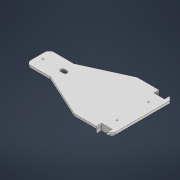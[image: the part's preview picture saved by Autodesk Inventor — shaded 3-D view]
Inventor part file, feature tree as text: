
AUTODESK INVENTOR PART (.ipt)
format: ipt  version: 2022 (Build 260153000, 153)  size: 181,760 bytes
history: native  units: in
note: dims shown in document units (in); Inventor stores cm internally (conversion verified against a paired STEP export)
features: sketch x9, extrude x6, fillet x2, chamfer x2, hole x1
ambient origin geometry x8: Origin, YZ Plane, XZ Plane, XY Plane, X Axis, Y Axis, Z Axis, Center Point
bodies: Solid1 (feature_tree)
feature tree (20):
  extrude  "Extrusion1"  Depth=0.7874in
  fillet  "Fillet1"  Radius=3.937in
  fillet  "Fillet2"  Radius=0.7874in
  chamfer  "Chamfer1"  Distance=1.5748in Angle=45.0deg
  chamfer  "Chamfer2"  Distance=1.5748in Angle=45.0deg
  sketch  "Sketch3"  dims[d19=1.9685in]
  sketch  "Sketch4"  dims[d20=1.9685in d21=1.5748in d22=0.0787in d23=45.0deg d24=1.5748in d25=0.0787in d26=45.0deg]
  extrude  "Extrusion2"  Depth=1.378in
  hole  "Hole1"  [1 undecoded]
  extrude  "Extrusion3"  Depth=3.937in
  extrude  "Extrusion4"  Depth=0.3937in
  extrude  "Extrusion5"  Depth=3.937in
  extrude  "Extrusion6"  Depth=2.3622in TaperAngle=0.0deg
  sketch  "Sketch1"  dims[d12=11.811in d13=13.7795in d16=3.937in d17=0.7874in d18=0.0in]
  sketch  "Sketch5"  dims[d27=2.3622in d28=1.378in]
  sketch  "Sketch6"  dims[d30=0.7874in d31=0.0in d33=1.9685in]
  sketch  "Sketch7"  dims[d34=0.3937in d35=0.2362in d36=0.1575in d37=0.0787in d38=90.0deg d39=0.315in d40=0.8108in d41=3.937in]
  sketch  "Sketch8"  dims[d42=1.5748in d43=0.0in d45=0.3937in]
  sketch  "Sketch9"  dims[d46=2.3622in d47=0.0in d48=3.937in]
  sketch  "Sketch10"  dims[d49=1.9685in d50=2.3622in d51=0.0in d53=7.874in d54=0.7874in d55=0.0in d29=0.0197in d32=0.0344in d44=0.0295in d52=0.0197in]
note: 1 required parameter value undecoded (feature->parameter linkage not recoverable at this tier; creation-order binding heuristic only, values carry confidence <= 0.55)
